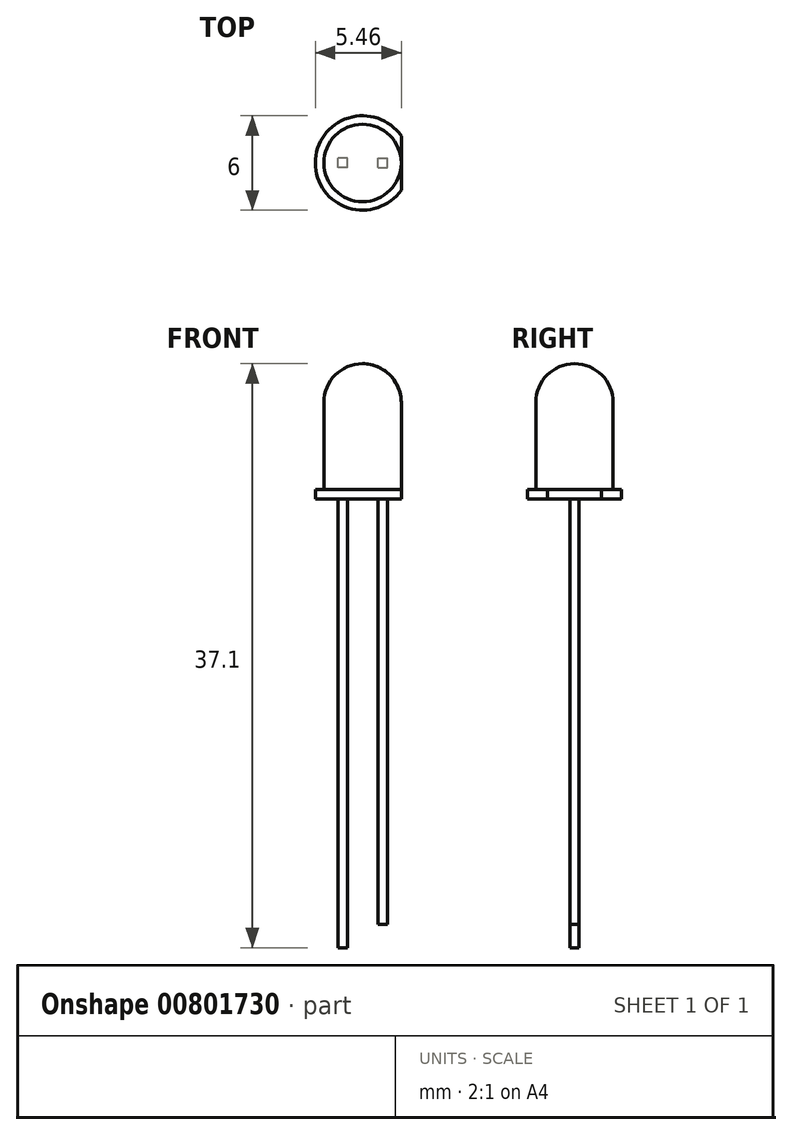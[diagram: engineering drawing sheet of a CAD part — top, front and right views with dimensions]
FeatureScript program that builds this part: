
annotation { "Feature Type Name" : "Feature", "Feature Type Description" : "" }
export const myFeature = defineFeature(function(context is Context, id is Id, definition is map)
    precondition{}
    {
        {
            var Q0;
            Q0=qCreatedBy(makeId("Front.planeOp"),FACE);
            var sketch = newSketch(context, id + "F0", { "sketchPlane" : qUnion([Q0])});
            skLineSegment(sketch, "E0.bottom", {"start": v(0, 0) * mm, "end": v(2.46, 0) * mm});
            skLineSegment(sketch, "E0.top", {"start": v(0, 8.6) * mm, "end": v(0, 8.6) * mm});
            skLineSegment(sketch, "E0.left", {"start": v(0, 0) * mm, "end": v(0, 8.6) * mm});
            skLineSegment(sketch, "E0.right", {"start": v(2.46, 0.6) * mm, "end": v(2.46, 6.14) * mm});
            skLineSegment(sketch, "E1.bottom", {"start": v(0, 0) * mm, "end": v(3, 0) * mm});
            skLineSegment(sketch, "E1.top", {"start": v(2.46, 0.6) * mm, "end": v(3, 0.6) * mm});
            skLineSegment(sketch, "E1.left", {"start": v(0, 0) * mm, "end": v(0, 0.6) * mm});
            skLineSegment(sketch, "E1.right", {"start": v(3, 0) * mm, "end": v(3, 0.6) * mm});
            skPoint(sketch, "E2.visualSharp", {"position": v(2.46, 8.6) * mm});
            skArc(sketch, "E2.filletArc", {"start": v(2.46, 6.14) * mm, "mid": v(1.74, 7.88) * mm, "end": v(0, 8.6) * mm});
            skSolve(sketch);
        }
        {
            var Q0;
            Q0 = qSketchRegion(id + "F0", true);
            var Q1;
            Q1=sQuery(id+"F0.wireOp",EDGE,"E0.left");
            revolve(context, id + "F1", {"surfaceOperationType" : NewSurfaceOperationType.NEW, "entities" : qUnion([Q0]), "axis" : qUnion([Q1]), "revolveType" : RevolveType.FULL});
        }
        {
            var Q0;
            Q0=makeQuery(id+"F1.opRevolve","SWEPT_FACE",FACE,{"disambiguationData":[OSD([sQuery(id+"F0.wireOp",EDGE,"E1.bottom")])]});
            var sketch = newSketch(context, id + "F2", { "sketchPlane" : qUnion([Q0])});
            skLineSegment(sketch, "E3", {"start": v(2.46, 0) * mm, "end": v(2.46, 1.72) * mm});
            skLineSegment(sketch, "E4", {"start": v(2.46, 0) * mm, "end": v(2.46, -1.72) * mm});
            skArc(sketch, "E5", {"start": v(2.46, -1.72) * mm, "mid": v(3, 0) * mm, "end": v(2.46, 1.72) * mm});
            skPoint(sketch, "E6", {"position": v(1.27, 0) * mm});
            skLineSegment(sketch, "E7.bottom", {"start": v(1.57, -0.3) * mm, "end": v(0.97, -0.3) * mm});
            skLineSegment(sketch, "E7.top", {"start": v(1.57, 0.3) * mm, "end": v(0.97, 0.3) * mm});
            skLineSegment(sketch, "E7.left", {"start": v(1.57, -0.3) * mm, "end": v(1.57, 0.3) * mm});
            skLineSegment(sketch, "E7.right", {"start": v(0.97, -0.3) * mm, "end": v(0.97, 0.3) * mm});
            skLineSegment(sketch, "E8.MirrorCS", {"start": v(-1.57, 0.3) * mm, "end": v(-0.97, 0.3) * mm});
            skLineSegment(sketch, "E9.MirrorCS", {"start": v(-0.97, -0.3) * mm, "end": v(-0.97, 0.3) * mm});
            skLineSegment(sketch, "E10.MirrorCS", {"start": v(-1.57, -0.3) * mm, "end": v(-0.97, -0.3) * mm});
            skLineSegment(sketch, "E11.MirrorCS", {"start": v(-1.57, -0.3) * mm, "end": v(-1.57, 0.3) * mm});
            skSolve(sketch);
        }
        {
            var Q0;
            Q0=makeQuery(id+"F2.imprint","IMPRINT",FACE,{"disambiguationData":[TD([[makeQuery(id+"F2.imprint","IMPRINT",EDGE,{"derivedFrom":sQuery(id+"F2.wireOp",EDGE,"E3")}),-1.0]])]});
            extrude(context, id + "F3", {"entities" : qUnion([Q0]), "operationType" : NewBodyOperationType.REMOVE, "oppositeDirection" : true, "depth" : 25.4 * mm, "offsetDistance" : 25.4 * mm});
        }
        {
            var Q0;
            Q0=makeQuery(id+"F2.imprint","IMPRINT",FACE,{"disambiguationData":[TD([[makeQuery(id+"F2.imprint","IMPRINT",EDGE,{"derivedFrom":sQuery(id+"F2.wireOp",EDGE,"E7.bottom")}),-1.0]])]});
            extrude(context, id + "F4", {"entities" : qUnion([Q0]), "depth" : 27 * mm, "offsetDistance" : 25.4 * mm});
        }
        {
            var Q0;
            Q0=makeQuery(id+"F2.imprint","IMPRINT",FACE,{"disambiguationData":[TD([[makeQuery(id+"F2.imprint","IMPRINT",EDGE,{"derivedFrom":sQuery(id+"F2.wireOp",EDGE,"E8.MirrorCS")}),-1.0]])]});
            extrude(context, id + "F5", {"entities" : qUnion([Q0]), "depth" : (27 + 1.5) * mm, "offsetDistance" : 25.4 * mm});
        }
        {
            var Q0;
            Q0=makeQuery(id+"F4.opExtrude","SWEPT_FACE",FACE,{"disambiguationData":[OSD([sQuery(id+"F2.wireOp",EDGE,"E7.top")])]});
            var sketch = newSketch(context, id + "F6", { "sketchPlane" : qUnion([Q0])});
            skLineSegment(sketch, "E12", {"start": v(0.97, 0) * mm, "end": v(0.97, 3.13) * mm});
            skLineSegment(sketch, "E13", {"start": v(0.97, 3.13) * mm, "end": v(-0.85, 4.73) * mm});
            skLineSegment(sketch, "E14", {"start": v(-0.85, 4.73) * mm, "end": v(1.57, 4.73) * mm});
            skLineSegment(sketch, "E15", {"start": v(1.57, 4.73) * mm, "end": v(1.57, 0) * mm});
            skLineSegment(sketch, "E16", {"start": v(0.97, 0) * mm, "end": v(1.57, 0) * mm});
            skSolve(sketch);
        }
        {
            var Q0;
            Q0 = qSketchRegion(id + "F6", true);
            extrude(context, id + "F7", {"entities" : qUnion([Q0]), "operationType" : NewBodyOperationType.ADD, "oppositeDirection" : true, "depth" : .6 * mm, "offsetDistance" : 25.4 * mm});
        }
        {
            var Q0;
            Q0=makeQuery(id+"F5.opExtrude","SWEPT_FACE",FACE,{"disambiguationData":[OSD([sQuery(id+"F2.wireOp",EDGE,"E8.MirrorCS")])]});
            var sketch = newSketch(context, id + "F8", { "sketchPlane" : qUnion([Q0])});
            skLineSegment(sketch, "E17", {"start": v(-1.57, 0) * mm, "end": v(-1.57, 4.72) * mm});
            skLineSegment(sketch, "E18", {"start": v(-1.57, 4.72) * mm, "end": v(0.2, 3.15) * mm});
            skLineSegment(sketch, "E19", {"start": v(0.2, 3.15) * mm, "end": v(-0.97, 3.15) * mm});
            skLineSegment(sketch, "E20", {"start": v(-0.97, 3.15) * mm, "end": v(-0.97, 0) * mm});
            skLineSegment(sketch, "E21", {"start": v(-0.97, 0) * mm, "end": v(-1.57, 0) * mm});
            skSolve(sketch);
        }
        {
            var Q0;
            Q0 = qSketchRegion(id + "F8", true);
            extrude(context, id + "F9", {"entities" : qUnion([Q0]), "operationType" : NewBodyOperationType.ADD, "oppositeDirection" : true, "depth" : .6 * mm, "offsetDistance" : 25.4 * mm});
        }
    });
